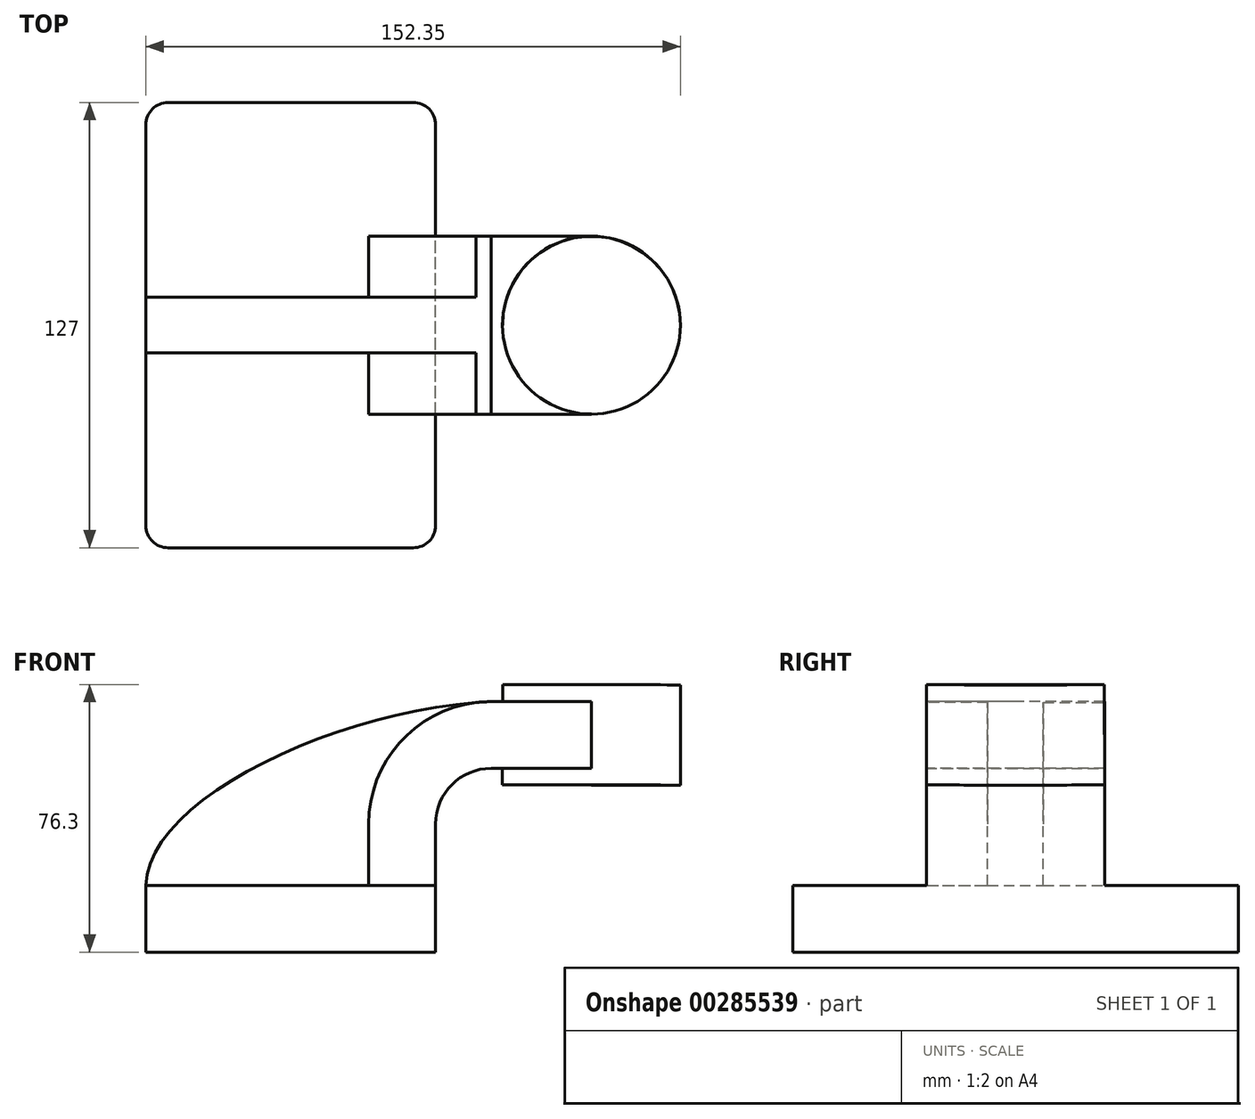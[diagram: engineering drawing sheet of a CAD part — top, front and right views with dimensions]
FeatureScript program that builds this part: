
annotation { "Feature Type Name" : "Feature", "Feature Type Description" : "" }
export const myFeature = defineFeature(function(context is Context, id is Id, definition is map)
    precondition{}
    {
        {
            var Q0;
            Q0=qCreatedBy(makeId("Front.planeOp"),FACE);
            var sketch = newSketch(context, id + "F0", { "sketchPlane" : qUnion([Q0])});
            skLineSegment(sketch, "E0.bottom", {"start": v(41.28, -9.52) * mm, "end": v(-41.28, -9.53) * mm});
            skLineSegment(sketch, "E0.top", {"start": v(41.28, 9.53) * mm, "end": v(-41.28, 9.53) * mm});
            skLineSegment(sketch, "E0.left", {"start": v(41.28, -9.52) * mm, "end": v(41.28, 9.53) * mm});
            skLineSegment(sketch, "E0.right", {"start": v(-41.28, -9.52) * mm, "end": v(-41.28, 9.53) * mm});
            skPoint(sketch, "E0.middle", {"position": v(0, 0) * mm});
            skLineSegment(sketch, "E1.bottom", {"start": v(60.27, 38.1) * mm, "end": v(111.07, 38.1) * mm});
            skLineSegment(sketch, "E1.top", {"start": v(60.27, 66.68) * mm, "end": v(111.07, 66.68) * mm});
            skLineSegment(sketch, "E1.left", {"start": v(60.27, 38.1) * mm, "end": v(60.27, 66.68) * mm});
            skLineSegment(sketch, "E1.right", {"start": v(111.07, 38.1) * mm, "end": v(111.07, 66.68) * mm});
            skPoint(sketch, "E1.middle", {"position": v(85.67, 52.39) * mm});
            skLineSegment(sketch, "E2", {"start": v(41.28, 9.53) * mm, "end": v(41.28, 27) * mm});
            skArc(sketch, "E3", {"start": v(41.27, 27) * mm, "mid": v(45.92, 38.23) * mm, "end": v(57.15, 42.88) * mm});
            skLineSegment(sketch, "E4", {"start": v(57.15, 42.88) * mm, "end": v(85.72, 42.88) * mm});
            skLineSegment(sketch, "E5.0", {"start": v(57.15, 61.93) * mm, "end": v(85.72, 61.93) * mm});
            skArc(sketch, "E5.1", {"start": v(22.23, 27) * mm, "mid": v(32.45, 51.7) * mm, "end": v(57.15, 61.93) * mm});
            skLineSegment(sketch, "E5.2", {"start": v(22.22, 9.53) * mm, "end": v(22.22, 27) * mm});
            skLineSegment(sketch, "E6", {"start": v(85.67, 38.1) * mm, "end": v(85.72, 66.68) * mm});
            skFitSpline(sketch, "E7", {"points": [v(-41.28, 9.53) * mm, v(57.15, 61.93) * mm], "startDerivative": vector(1.14, 73.82) * mm, "endDerivative": vector(130.87, 6) * mm});
            skSolve(sketch);
        }
        {
            var Q0;
            Q0=makeQuery(id+"F0.imprint","IMPRINT",FACE,{"disambiguationData":[TD([[makeQuery(id+"F0.imprint","IMPRINT",EDGE,{"derivedFrom":sQuery(id+"F0.wireOp",EDGE,"E0.bottom")}),-1.0]])]});
            extrude(context, id + "F1", {"entities" : qUnion([Q0]), "endBound" : BoundingType.SYMMETRIC, "depth" : 127 * mm});
        }
        {
            var Q0;
            {var subQ1=sQuery(id+"F0.wireOp",EDGE,"E2");Q0=makeQuery(id+"F0.imprint","IMPRINT",FACE,{"disambiguationData":[TD([[makeQuery(id+"F0.imprint","IMPRINT",EDGE,{"derivedFrom":subQ1}),1.0]])]});}
            var Q1;
            {var subQ0=sQuery(id+"F0.wireOp",EDGE,"E4");var subQ1=sQuery(id+"F0.wireOp",EDGE,"E1.left");var subQ2=makeQuery(id+"F0.imprint","INTERSECT",VERTEX,{"derivedFrom":[subQ1,subQ0]});Q1=makeQuery(id+"F0.imprint","IMPRINT",FACE,{"disambiguationData":[TD([[makeQuery(id+"F0.imprint","IMPRINT",EDGE,{"disambiguationData":[TD([[subQ2,-1.0]])],"derivedFrom":subQ1}),-1.0]])]});}
            extrude(context, id + "F2", {"entities" : qUnion([Q0, Q1]), "operationType" : NewBodyOperationType.ADD, "endBound" : BoundingType.SYMMETRIC, "depth" : 50.8 * mm});
        }
        {
            var Q0;
            {var subQ3=sQuery(id+"F0.wireOp",EDGE,"E5.2");Q0=makeQuery(id+"F0.imprint","IMPRINT",FACE,{"disambiguationData":[TD([[makeQuery(id+"F0.imprint","IMPRINT",EDGE,{"derivedFrom":subQ3}),1.0]])]});}
            extrude(context, id + "F3", {"entities" : qUnion([Q0]), "operationType" : NewBodyOperationType.ADD, "endBound" : BoundingType.SYMMETRIC, "depth" : 15.88 * mm});
        }
        {
            var Q0;
            {var subQ4=sQuery(id+"F0.wireOp",EDGE,"E1.right");Q0=makeQuery(id+"F0.imprint","IMPRINT",FACE,{"disambiguationData":[TD([[makeQuery(id+"F0.imprint","IMPRINT",EDGE,{"derivedFrom":subQ4}),1.0]])]});}
            var Q1;
            Q1=sQuery(id+"F0.wireOp",EDGE,"E6");
            revolve(context, id + "F4", {"operationType" : NewBodyOperationType.ADD, "entities" : qUnion([Q0]), "axis" : qUnion([Q1]), "revolveType" : RevolveType.FULL});
        }
        {
            var Q0;
            Q0=makeQuery(id+"F1.opExtrude","CAP_EDGE",EDGE,{"disambiguationData":[OSD([sQuery(id+"F0.wireOp",EDGE,"E0.left")])],"isStart":false});
            var Q1;
            Q1=makeQuery(id+"F1.opExtrude","CAP_EDGE",EDGE,{"disambiguationData":[OSD([sQuery(id+"F0.wireOp",EDGE,"E0.left")])],"isStart":true});
            var Q2;
            Q2=makeQuery(id+"F1.opExtrude","CAP_EDGE",EDGE,{"disambiguationData":[OSD([sQuery(id+"F0.wireOp",EDGE,"E0.right")])],"isStart":true});
            var Q3;
            Q3=makeQuery(id+"F1.opExtrude","CAP_EDGE",EDGE,{"disambiguationData":[OSD([sQuery(id+"F0.wireOp",EDGE,"E0.right")])],"isStart":false});
            fillet(context, id + "F5", {"entities" : qUnion([Q0, Q1, Q2, Q3]), "radius" : 6.35 * mm, "tangentPropagation" : true, "allowEdgeOverflow" : false});
        }
    });
